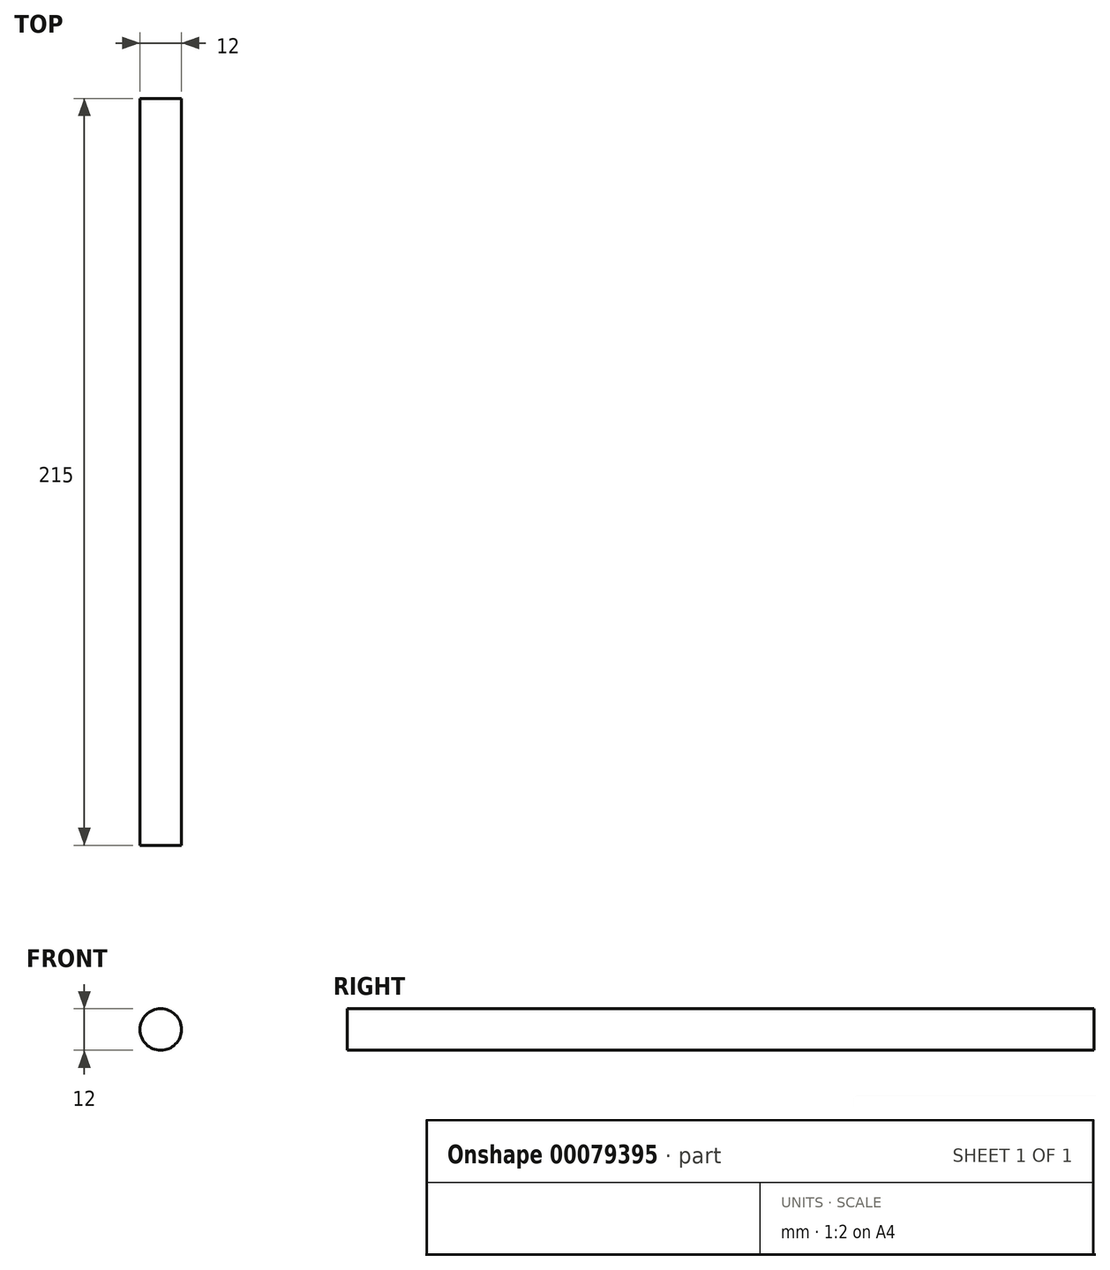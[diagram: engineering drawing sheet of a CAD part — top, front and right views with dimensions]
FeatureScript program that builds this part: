
annotation { "Feature Type Name" : "Feature", "Feature Type Description" : "" }
export const myFeature = defineFeature(function(context is Context, id is Id, definition is map)
    precondition{}
    {
        {
            var Q0;
            Q0=qCreatedBy(makeId("Front.planeOp"),FACE);
            var sketch = newSketch(context, id + "F0", { "sketchPlane" : qUnion([Q0])});
            skCircle(sketch, "E0", {"center": v(0, 0) * mm, "radius": 6 * mm});
            skSolve(sketch);
        }
        {
            var Q0;
            Q0 = qSketchRegion(id + "F0", true);
            extrude(context, id + "F1", {"entities" : qUnion([Q0]), "depth" : 215 * mm});
        }
    });
